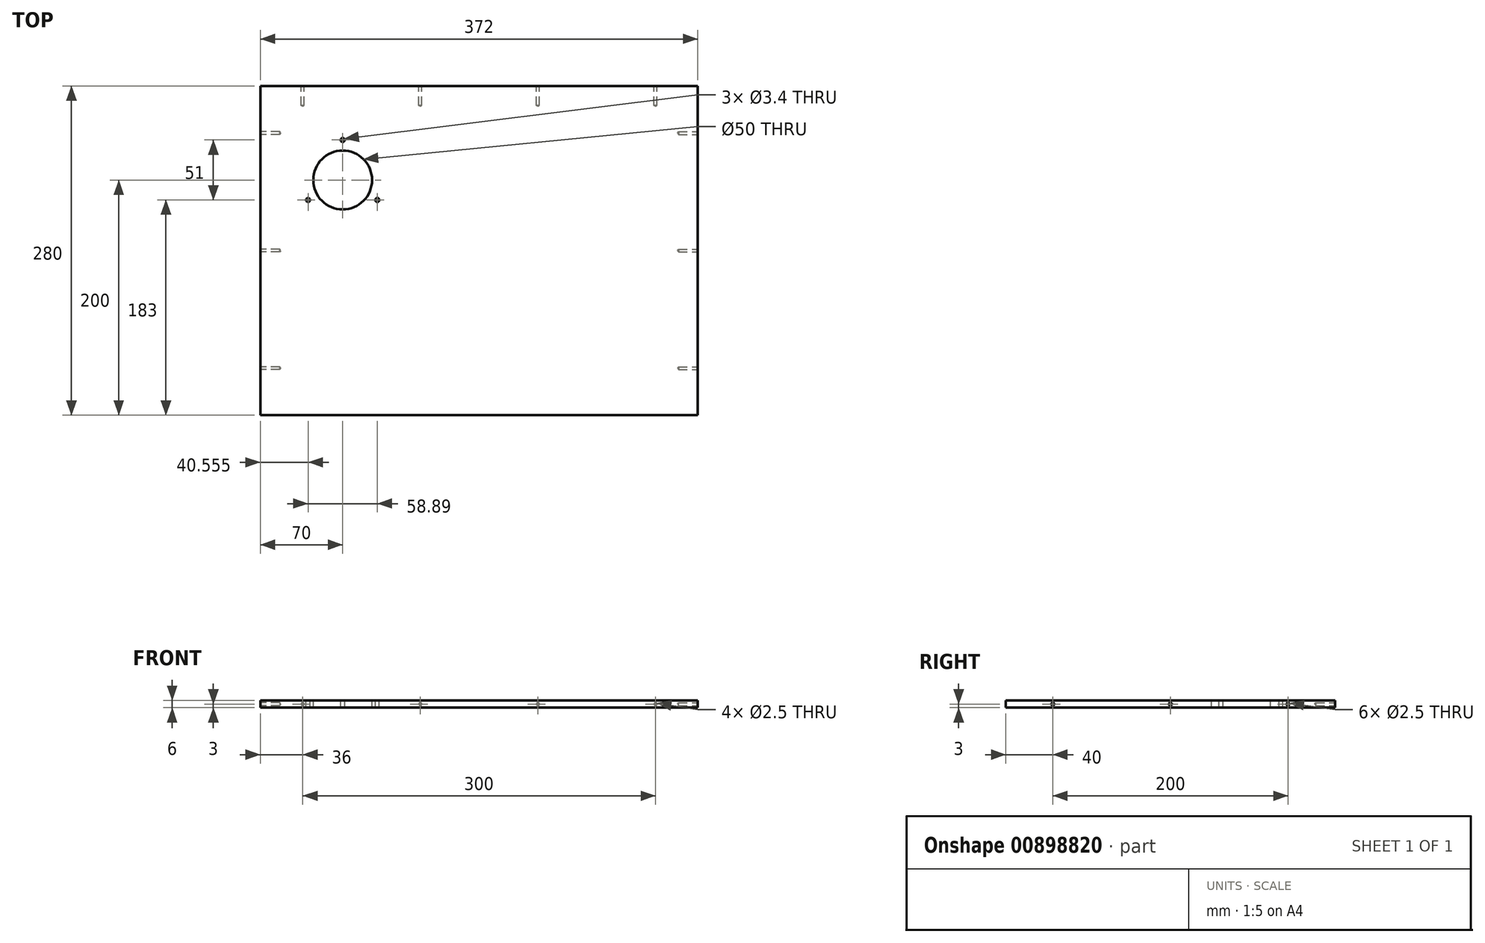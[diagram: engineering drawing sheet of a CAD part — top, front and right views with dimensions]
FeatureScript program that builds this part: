
annotation { "Feature Type Name" : "Feature", "Feature Type Description" : "" }
export const myFeature = defineFeature(function(context is Context, id is Id, definition is map)
    precondition{}
    {
        {
            var Q0;
            Q0=qCreatedBy(makeId("Top.planeOp"),FACE);
            var sketch = newSketch(context, id + "F0", { "sketchPlane" : qUnion([Q0])});
            skLineSegment(sketch, "E0.bottom", {"start": v(186, 140) * mm, "end": v(-186, 140) * mm});
            skLineSegment(sketch, "E0.top", {"start": v(186, -140) * mm, "end": v(-186, -140) * mm});
            skLineSegment(sketch, "E0.left", {"start": v(186, 140) * mm, "end": v(186, -140) * mm});
            skLineSegment(sketch, "E0.right", {"start": v(-186, 140) * mm, "end": v(-186, -140) * mm});
            skPoint(sketch, "E0.middle", {"position": v(0, 0) * mm});
            skSolve(sketch);
        }
        {
            var Q0;
            Q0=makeQuery(id+"F0.imprint","IMPRINT",FACE,{"disambiguationData":[TD([[makeQuery(id+"F0.imprint","IMPRINT",EDGE,{"derivedFrom":sQuery(id+"F0.wireOp",EDGE,"E0.bottom")}),1.0]])]});
            extrude(context, id + "F1", {"entities" : qUnion([Q0]), "depth" : 6 * mm, "offsetDistance" : 25 * mm});
        }
        {
            var Q0;
            Q0=makeQuery(id+"F1.opExtrude","CAP_FACE",FACE,{"disambiguationData":[OSD([sQuery(id+"F0.wireOp",EDGE,"E0.bottom"),sQuery(id+"F0.wireOp",EDGE,"E0.top"),sQuery(id+"F0.wireOp",EDGE,"E0.left"),sQuery(id+"F0.wireOp",EDGE,"E0.right")])],"isStart":false});
            var sketch = newSketch(context, id + "F2", { "sketchPlane" : qUnion([Q0])});
            skCircle(sketch, "E1", {"center": v(-116, 60) * mm, "radius": 25 * mm});
            skCircle(sketch, "E2", {"center": v(-116, 60) * mm, "radius": 34 * mm, "construction": true});
            skPoint(sketch, "E3", {"position": v(-116, 94) * mm});
            skPoint(sketch, "E4", {"position": v(-145.44, 43) * mm});
            skPoint(sketch, "E5", {"position": v(-86.56, 43) * mm});
            skLineSegment(sketch, "E6", {"start": v(-116, 94) * mm, "end": v(-116, 60) * mm, "construction": true});
            skLineSegment(sketch, "E7", {"start": v(-116, 60) * mm, "end": v(-145.44, 43) * mm, "construction": true});
            skLineSegment(sketch, "E8", {"start": v(-116, 60) * mm, "end": v(-86.56, 43) * mm, "construction": true});
            skSolve(sketch);
        }
        {
            var Q0;
            Q0=makeQuery(id+"F2.imprint","IMPRINT",FACE,{"disambiguationData":[TD([[makeQuery(id+"F2.imprint","IMPRINT",EDGE,{"derivedFrom":sQuery(id+"F2.wireOp",EDGE,"E1")}),1.0]])]});
            extrude(context, id + "F3", {"entities" : qUnion([Q0]), "oppositeDirection" : true, "depth" : 6 * mm, "offsetDistance" : 25 * mm});
        }
        {
            var Q0;
            Q0=makeQuery(id+"F3.opExtrude","SWEPT_BODY",BODY,{"disambiguationData":[OSD([sQuery(id+"F2.wireOp",EDGE,"E1")])]});
            var Q1;
            Q1=makeQuery(id+"F1.opExtrude","SWEPT_BODY",BODY,{"disambiguationData":[OSD([sQuery(id+"F0.wireOp",EDGE,"E0.bottom"),sQuery(id+"F0.wireOp",EDGE,"E0.top"),sQuery(id+"F0.wireOp",EDGE,"E0.left"),sQuery(id+"F0.wireOp",EDGE,"E0.right")])]});
            booleanBodies(context, id + "F4", {"operationType" : BooleanOperationType.SUBTRACTION, "tools" : qUnion([Q0]), "targets" : qUnion([Q1])});
        }
        {
            var Q0;
            Q0=sQuery(id+"F2.wireOp",VERTEX,"E3");
            var Q1;
            Q1=sQuery(id+"F2.wireOp",VERTEX,"E4");
            var Q2;
            Q2=sQuery(id+"F2.wireOp",VERTEX,"E5");
            var Q3;
            Q3=makeQuery(id+"F1.opExtrude","SWEPT_BODY",BODY,{"disambiguationData":[OSD([sQuery(id+"F0.wireOp",EDGE,"E0.bottom"),sQuery(id+"F0.wireOp",EDGE,"E0.top"),sQuery(id+"F0.wireOp",EDGE,"E0.left"),sQuery(id+"F0.wireOp",EDGE,"E0.right")])]});
            hole(context, id + "F5", {"style" : HoleStyle.SIMPLE, "endStyle" : HoleEndStyle.THROUGH, "standardTappedOrClearance" : lookupTablePath({ "fit" : "Normal", "standard" : "ISO", "size" : "M3", "type" : "Clearance" }), "standardBlindInLast" : lookupTablePath({ "fit" : "Normal", "standard" : "ISO", "size" : "M3", "type" : "Clearance" }), "holeDiameter" : 3.4 * mm, "majorDiameter" : 3 * mm, "tappedDepth" : 15 * mm, "tapClearance" : 3, "locations" : qUnion([Q0, Q1, Q2]), "scope" : qUnion([Q3])});
        }
        {
            var Q0;
            Q0=makeQuery(id+"F1.opExtrude","SWEPT_FACE",FACE,{"disambiguationData":[OSD([sQuery(id+"F0.wireOp",EDGE,"E0.left")])]});
            var sketch = newSketch(context, id + "F6", { "sketchPlane" : qUnion([Q0])});
            skPoint(sketch, "E9", {"position": v(-100, 3) * mm});
            skPoint(sketch, "E10", {"position": v(0, 3) * mm});
            skPoint(sketch, "E11", {"position": v(100, 3) * mm});
            skSolve(sketch);
        }
        {
            var Q0;
            Q0=makeQuery(id+"F1.opExtrude","SWEPT_FACE",FACE,{"disambiguationData":[OSD([sQuery(id+"F0.wireOp",EDGE,"E0.right")])]});
            var sketch = newSketch(context, id + "F7", { "sketchPlane" : qUnion([Q0])});
            skPoint(sketch, "E12", {"position": v(100, 3) * mm});
            skPoint(sketch, "E13", {"position": v(0, 3) * mm});
            skPoint(sketch, "E14", {"position": v(-100, 3) * mm});
            skSolve(sketch);
        }
        {
            var Q0;
            Q0=makeQuery(id+"F1.opExtrude","SWEPT_FACE",FACE,{"disambiguationData":[OSD([sQuery(id+"F0.wireOp",EDGE,"E0.bottom")])]});
            var sketch = newSketch(context, id + "F8", { "sketchPlane" : qUnion([Q0])});
            skPoint(sketch, "E15", {"position": v(-150, 3) * mm});
            skPoint(sketch, "E16", {"position": v(-50, 3) * mm});
            skPoint(sketch, "E17", {"position": v(50, 3) * mm});
            skPoint(sketch, "E18", {"position": v(150, 3) * mm});
            skSolve(sketch);
        }
        {
            var Q0;
            Q0=sQuery(id+"F6.wireOp",VERTEX,"E9");
            var Q1;
            Q1=sQuery(id+"F6.wireOp",VERTEX,"E10");
            var Q2;
            Q2=sQuery(id+"F6.wireOp",VERTEX,"E11");
            var Q3;
            Q3=sQuery(id+"F8.wireOp",VERTEX,"E15");
            var Q4;
            Q4=sQuery(id+"F8.wireOp",VERTEX,"E16");
            var Q5;
            Q5=sQuery(id+"F8.wireOp",VERTEX,"E17");
            var Q6;
            Q6=sQuery(id+"F7.wireOp",VERTEX,"E14");
            var Q7;
            Q7=sQuery(id+"F7.wireOp",VERTEX,"E13");
            var Q8;
            Q8=sQuery(id+"F7.wireOp",VERTEX,"E12");
            var Q9;
            Q9=sQuery(id+"F8.wireOp",VERTEX,"058461e3-6349-40f5-93f5-0512fa832c00");
            var Q10;
            Q10=makeQuery(id+"F1.opExtrude","SWEPT_BODY",BODY,{"disambiguationData":[OSD([sQuery(id+"F0.wireOp",EDGE,"E0.bottom"),sQuery(id+"F0.wireOp",EDGE,"E0.top"),sQuery(id+"F0.wireOp",EDGE,"E0.left"),sQuery(id+"F0.wireOp",EDGE,"E0.right")])]});
            hole(context, id + "F9", {"style" : HoleStyle.SIMPLE, "endStyle" : HoleEndStyle.BLIND, "standardTappedOrClearance" : lookupTablePath({ "standard" : "ISO", "engagement" : "75%", "pitch" : "0.5 mm", "size" : "M3", "type" : "Tapped" }), "standardBlindInLast" : lookupTablePath({ "standard" : "ISO", "engagement" : "75%", "pitch" : "0.5 mm", "size" : "M3", "type" : "Tapped" }), "holeDiameter" : 2.5 * mm, "majorDiameter" : 3 * mm, "showTappedDepth" : true, "holeDepth" : 16.5 * mm, "tappedDepth" : 15 * mm, "tapClearance" : 3, "locations" : qUnion([Q0, Q1, Q2, Q3, Q4, Q5, Q6, Q7, Q8, Q9]), "scope" : qUnion([Q10])});
        }
        {
            var Q0;
            Q0=sQuery(id+"F8.wireOp",VERTEX,"E18");
            var Q1;
            Q1=makeQuery(id+"F1.opExtrude","SWEPT_BODY",BODY,{"disambiguationData":[OSD([sQuery(id+"F0.wireOp",EDGE,"E0.bottom"),sQuery(id+"F0.wireOp",EDGE,"E0.top"),sQuery(id+"F0.wireOp",EDGE,"E0.left"),sQuery(id+"F0.wireOp",EDGE,"E0.right")])]});
            hole(context, id + "F10", {"style" : HoleStyle.SIMPLE, "endStyle" : HoleEndStyle.BLIND, "standardTappedOrClearance" : lookupTablePath({ "standard" : "ISO", "engagement" : "75%", "pitch" : "0.5 mm", "size" : "M3", "type" : "Tapped" }), "standardBlindInLast" : lookupTablePath({ "standard" : "ISO", "fit" : "Normal", "engagement" : "75%", "pitch" : "0.5 mm", "size" : "M3", "type" : "Clearance & tapped" }), "holeDiameter" : 2.5 * mm, "majorDiameter" : 3 * mm, "showTappedDepth" : true, "holeDepth" : 16.5 * mm, "tappedDepth" : 15 * mm, "tapClearance" : 3, "locations" : qUnion([Q0]), "scope" : qUnion([Q1])});
        }
    });
